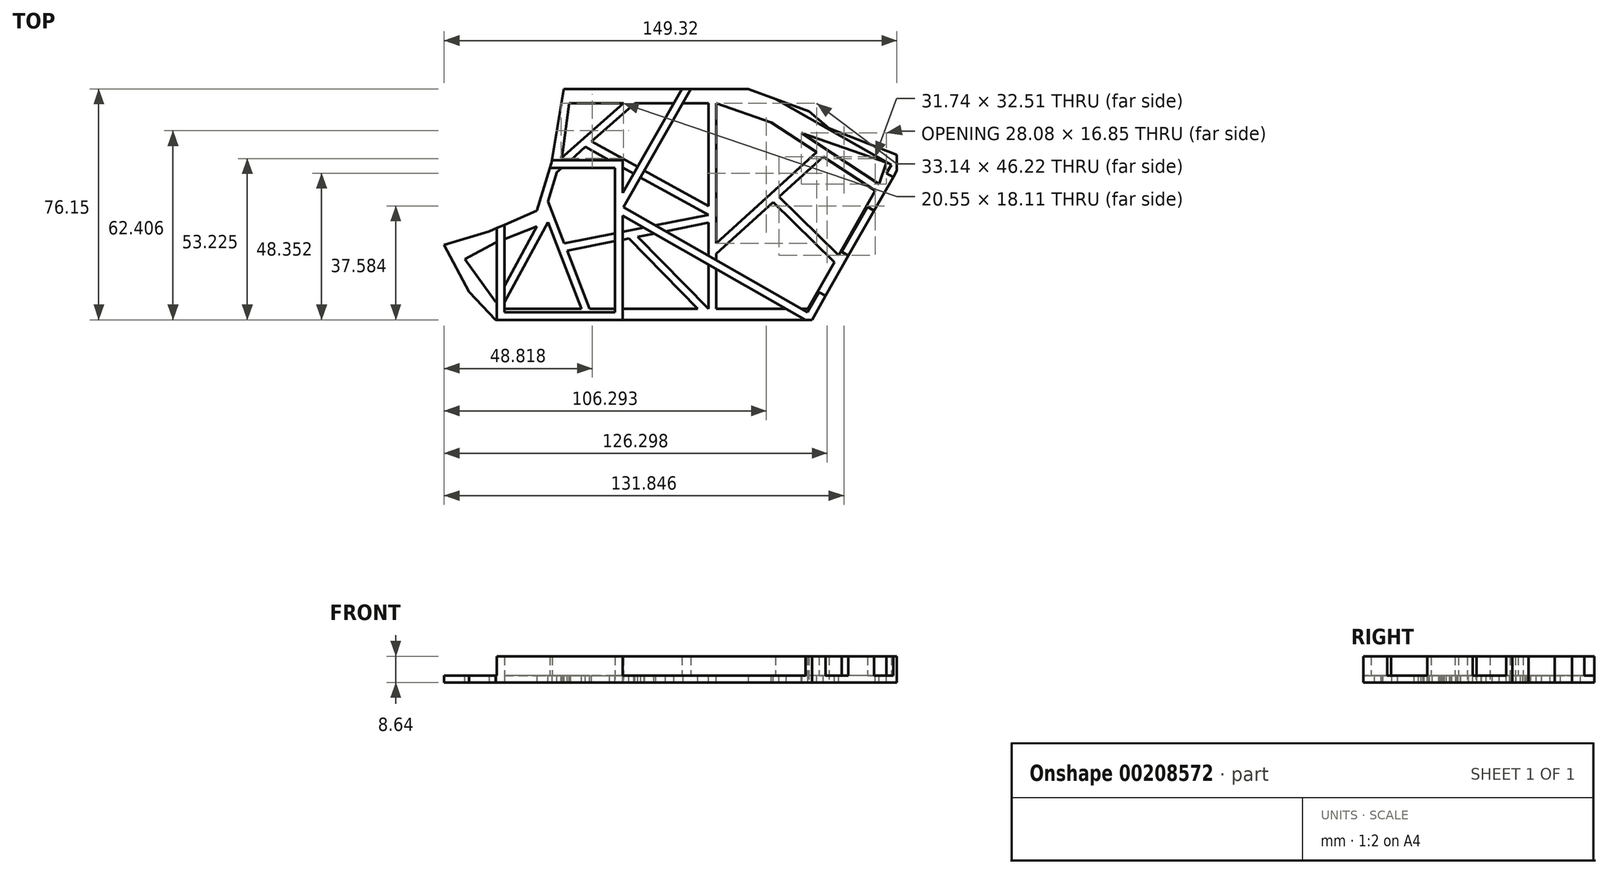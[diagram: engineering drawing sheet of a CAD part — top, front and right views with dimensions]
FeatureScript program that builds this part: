
annotation { "Feature Type Name" : "Feature", "Feature Type Description" : "" }
export const myFeature = defineFeature(function(context is Context, id is Id, definition is map)
    precondition{}
    {
        {
            var Q0;
            Q0=qCreatedBy(makeId("Top.planeOp"),FACE);
            var sketch = newSketch(context, id + "F0", { "sketchPlane" : qUnion([Q0])});
            skLineSegment(sketch, "E0", {"start": v(-31, -29.13) * mm, "end": v(-39.75, -19.88) * mm});
            skLineSegment(sketch, "E1", {"start": v(-39.75, -19.88) * mm, "end": v(-48, -4.38) * mm});
            skLineSegment(sketch, "E2", {"start": v(-48, -4.38) * mm, "end": v(-33.25, 0) * mm});
            skLineSegment(sketch, "E3", {"start": v(-33.25, 0) * mm, "end": v(-17.5, 6.88) * mm});
            skLineSegment(sketch, "E4", {"start": v(-17.5, 6.88) * mm, "end": v(-12.44, 23.38) * mm});
            skLineSegment(sketch, "E5", {"start": v(-12.44, 23.38) * mm, "end": v(-10.46, 47.02) * mm});
            skLineSegment(sketch, "E6", {"start": v(-10.46, 47.02) * mm, "end": v(19.98, 47.02) * mm});
            skLineSegment(sketch, "E7", {"start": v(19.98, 47.02) * mm, "end": v(21.89, 47.02) * mm});
            skLineSegment(sketch, "E8", {"start": v(21.89, 47.02) * mm, "end": v(52.33, 47.02) * mm});
            skLineSegment(sketch, "E9", {"start": v(50.42, 47.02) * mm, "end": v(52.33, 47.02) * mm});
            skLineSegment(sketch, "E10", {"start": v(78.88, 34.03) * mm, "end": v(101.32, 25.34) * mm});
            skLineSegment(sketch, "E11", {"start": v(101.32, 25.34) * mm, "end": v(101.32, 20.06) * mm});
            skLineSegment(sketch, "E12", {"start": v(73.3, -29.13) * mm, "end": v(-31, -29.13) * mm});
            skLineSegment(sketch, "E13", {"start": v(-10.46, 47.02) * mm, "end": v(-10.46, 53.42) * mm});
            skLineSegment(sketch, "E14", {"start": v(-10.46, 53.42) * mm, "end": v(-8.56, 53.42) * mm});
            skLineSegment(sketch, "E15", {"start": v(-8.56, 53.42) * mm, "end": v(-8.56, 47.02) * mm});
            skLineSegment(sketch, "E16", {"start": v(19.98, 47.02) * mm, "end": v(19.98, 53.42) * mm});
            skLineSegment(sketch, "E17", {"start": v(19.98, 53.42) * mm, "end": v(21.89, 53.42) * mm});
            skLineSegment(sketch, "E18", {"start": v(21.89, 53.42) * mm, "end": v(21.89, 47.02) * mm});
            skLineSegment(sketch, "E19", {"start": v(52.33, 47.02) * mm, "end": v(53.46, 53.42) * mm});
            skLineSegment(sketch, "E20", {"start": v(50.42, 53.42) * mm, "end": v(53.46, 53.42) * mm});
            skLineSegment(sketch, "E21", {"start": v(50.42, 53.42) * mm, "end": v(50.42, 47.02) * mm});
            skLineSegment(sketch, "E22", {"start": v(101.32, 25.34) * mm, "end": v(102.22, 27.67) * mm});
            skLineSegment(sketch, "E23", {"start": v(-8.56, 47.02) * mm, "end": v(-12.44, 23.38) * mm});
            skLineSegment(sketch, "E24", {"start": v(101.32, 20.06) * mm, "end": v(73.3, -29.13) * mm});
            skLineSegment(sketch, "E25", {"start": v(52.33, 47.02) * mm, "end": v(72.33, 39.67) * mm});
            skLineSegment(sketch, "E26", {"start": v(102.22, 27.67) * mm, "end": v(103.95, 27) * mm});
            skLineSegment(sketch, "E27", {"start": v(103.95, 27) * mm, "end": v(101.32, 20.06) * mm});
            skLineSegment(sketch, "E28", {"start": v(72.33, 39.67) * mm, "end": v(78.88, 34.03) * mm});
            skSolve(sketch);
        }
        {
            var Q0;
            Q0=makeQuery(id+"F0.imprint","IMPRINT",FACE,{"disambiguationData":[TD([[makeQuery(id+"F0.imprint","IMPRINT",EDGE,{"derivedFrom":sQuery(id+"F0.wireOp",EDGE,"E0")}),-1.0]])]});
            var Q1;
            Q1=makeQuery(id+"F0.imprint","IMPRINT",FACE,{"disambiguationData":[TD([[makeQuery(id+"F0.imprint","IMPRINT",EDGE,{"derivedFrom":sQuery(id+"F0.wireOp",EDGE,"Gi2NU1hI-RyGe-3cBe-QKJR-tDSeOLIxTJu2")}),-1.0]])]});
            extrude(context, id + "F1", {"entities" : qUnion([Q0, Q1]), "depth" : 2.3 * mm});
        }
        {
            var Q0;
            Q0=makeQuery(id+"F1.opExtrude","CAP_FACE",FACE,{"disambiguationData":[OSD([sQuery(id+"F0.wireOp",EDGE,"E0"),sQuery(id+"F0.wireOp",EDGE,"E1"),sQuery(id+"F0.wireOp",EDGE,"E2"),sQuery(id+"F0.wireOp",EDGE,"E3"),sQuery(id+"F0.wireOp",EDGE,"E4"),sQuery(id+"F0.wireOp",EDGE,"E6"),sQuery(id+"F0.wireOp",EDGE,"E7"),sQuery(id+"F0.wireOp",EDGE,"E8"),sQuery(id+"F0.wireOp",EDGE,"E9"),sQuery(id+"F0.wireOp",EDGE,"E10"),sQuery(id+"F0.wireOp",EDGE,"E11"),sQuery(id+"F0.wireOp",EDGE,"E12"),sQuery(id+"F0.wireOp",EDGE,"E23"),sQuery(id+"F0.wireOp",EDGE,"E24"),sQuery(id+"F0.wireOp",EDGE,"E25"),sQuery(id+"F0.wireOp",EDGE,"E28")])],"isStart":false});
            var sketch = newSketch(context, id + "F2", { "sketchPlane" : qUnion([Q0])});
            skLineSegment(sketch, "E29", {"start": v(71.83, -26.59) * mm, "end": v(99.48, 21.97) * mm});
            skLineSegment(sketch, "E30", {"start": v(99.48, 21.97) * mm, "end": v(61.26, 43.74) * mm});
            skLineSegment(sketch, "E31", {"start": v(72.33, 39.67) * mm, "end": v(101.32, 25.34) * mm});
            skLineSegment(sketch, "E32", {"start": v(72.33, 39.67) * mm, "end": v(61.26, 43.74) * mm});
            skLineSegment(sketch, "E33", {"start": v(71.83, -26.59) * mm, "end": v(11.13, 7.98) * mm});
            skLineSegment(sketch, "E34", {"start": v(8.37, 21.04) * mm, "end": v(8.37, -26.59) * mm});
            skLineSegment(sketch, "E35", {"start": v(8.37, 21.04) * mm, "end": v(-28.14, 21.04) * mm});
            skLineSegment(sketch, "E36", {"start": v(-28.14, 21.04) * mm, "end": v(-28.14, -26.59) * mm});
            skLineSegment(sketch, "E37", {"start": v(-28.14, -29.13) * mm, "end": v(8.37, -29.13) * mm});
            skLineSegment(sketch, "E38", {"start": v(-30.68, -29.13) * mm, "end": v(-30.68, 23.58) * mm});
            skLineSegment(sketch, "E39", {"start": v(-30.68, 23.58) * mm, "end": v(10.9, 23.58) * mm});
            skLineSegment(sketch, "E40", {"start": v(-28.14, -29.13) * mm, "end": v(-30.68, -29.13) * mm});
            skLineSegment(sketch, "E41", {"start": v(10.9, -29.13) * mm, "end": v(8.37, -29.13) * mm});
            skLineSegment(sketch, "E42", {"start": v(52.33, 47.02) * mm, "end": v(61.26, 43.74) * mm});
            skLineSegment(sketch, "E43", {"start": v(101.32, 25.34) * mm, "end": v(101.32, 20.06) * mm});
            skLineSegment(sketch, "E44", {"start": v(101.32, 20.06) * mm, "end": v(73.3, -29.13) * mm});
            skLineSegment(sketch, "E45", {"start": v(73.3, -29.13) * mm, "end": v(71.16, -29.13) * mm});
            skPoint(sketch, "E46.startSnap0", {"position": v(-25.38, 3.44) * mm});
            skLineSegment(sketch, "E47", {"start": v(-12.38, 23.58) * mm, "end": v(-13.16, 21.04) * mm});
            skLineSegment(sketch, "E48", {"start": v(8.37, -29.13) * mm, "end": v(10.9, -29.13) * mm});
            skPoint(sketch, "E49.orphan", {"position": v(8.37, 9.55) * mm});
            skLineSegment(sketch, "E50", {"start": v(-28.14, 2.23) * mm, "end": v(-30.68, 1.12) * mm});
            skLineSegment(sketch, "E51", {"start": v(71.16, -29.13) * mm, "end": v(10.9, 5.19) * mm});
            skLineSegment(sketch, "E52.trimOffspring", {"start": v(10.9, 5.19) * mm, "end": v(10.9, -29.13) * mm});
            skLineSegment(sketch, "E53", {"start": v(10.9, 23.58) * mm, "end": v(10.9, 12.72) * mm});
            skLineSegment(sketch, "E54", {"start": v(30.44, 47.02) * mm, "end": v(10.9, 12.72) * mm});
            skLineSegment(sketch, "E55", {"start": v(11.13, 7.98) * mm, "end": v(33.37, 47.02) * mm});
            skLineSegment(sketch, "E56", {"start": v(33.37, 47.02) * mm, "end": v(30.44, 47.02) * mm});
            skLineSegment(sketch, "E57", {"start": v(100.12, 17.96) * mm, "end": v(97.91, 19.21) * mm});
            skLineSegment(sketch, "E58", {"start": v(93.83, 6.92) * mm, "end": v(91.63, 8.18) * mm});
            skLineSegment(sketch, "E59", {"start": v(85.35, -7.98) * mm, "end": v(83.14, -6.72) * mm});
            skLineSegment(sketch, "E60", {"start": v(77.8, -21.22) * mm, "end": v(75.6, -19.96) * mm});
            skLineSegment(sketch, "E61", {"start": v(-28.14, -26.59) * mm, "end": v(8.37, -26.59) * mm});
            skSolve(sketch);
        }
        {
            var Q0;
            {var subQ0=sQuery(id+"F0.wireOp",EDGE,"E1");Q0=makeQuery(id+"FvVTFxztvHye57Z_1.boolean.opBoolean","MERGE",FACE,{"derivedFrom":[makeQuery(id+"F1.opExtrude","CAP_FACE",FACE,{"disambiguationData":[OSD([sQuery(id+"F0.wireOp",EDGE,"E0"),subQ0,sQuery(id+"F0.wireOp",EDGE,"E2"),sQuery(id+"F0.wireOp",EDGE,"E3"),sQuery(id+"F0.wireOp",EDGE,"E4"),sQuery(id+"F0.wireOp",EDGE,"E6"),sQuery(id+"F0.wireOp",EDGE,"E7"),sQuery(id+"F0.wireOp",EDGE,"E8"),sQuery(id+"F0.wireOp",EDGE,"E9"),sQuery(id+"F0.wireOp",EDGE,"E10"),sQuery(id+"F0.wireOp",EDGE,"E11"),sQuery(id+"F0.wireOp",EDGE,"E12"),sQuery(id+"F0.wireOp",EDGE,"E23"),sQuery(id+"F0.wireOp",EDGE,"E24"),sQuery(id+"F0.wireOp",EDGE,"E25"),sQuery(id+"F0.wireOp",EDGE,"fd09a7df-8c5c-424c-a2e8-465319626604.filletArc"),sQuery(id+"F0.wireOp",EDGE,"Gi2NU1hI-RyGe-3cBe-QKJR-tDSeOLIxTJu2"),sQuery(id+"F0.wireOp",EDGE,"a5mEmpnJ-nNCN-zs6l-W8Vb-FC9yOFSv0VO3"),sQuery(id+"F0.wireOp",EDGE,"UyYbmhtn-IZG5-9lsr-55o4-O6naXDKF2BvH"),sQuery(id+"F0.wireOp",EDGE,"27fbc29f-c9e2-412b-bed3-38be6e3044b4.trimOffspring")])],"isStart":false}),makeQuery(id+"FvVTFxztvHye57Z_1.opExtrude","SWEPT_FACE",FACE,{"disambiguationData":[OSD([subQ0]),TDD([makeQuery(id+"F1.opExtrude","CAP_EDGE",EDGE,{"disambiguationData":[OSD([subQ0])],"isStart":false})])]})]});}
            var sketch = newSketch(context, id + "F3", { "sketchPlane" : qUnion([Q0])});
            skLineSegment(sketch, "E62", {"start": v(-6.84, 42.33) * mm, "end": v(41.72, 42.33) * mm});
            skLineSegment(sketch, "E63", {"start": v(41.72, 42.33) * mm, "end": v(97.89, 22.71) * mm});
            skLineSegment(sketch, "E64", {"start": v(97.89, 22.71) * mm, "end": v(95.43, 15.67) * mm});
            skLineSegment(sketch, "E65", {"start": v(95.43, 15.67) * mm, "end": v(71.96, -25.53) * mm});
            skLineSegment(sketch, "E66", {"start": v(71.96, -25.53) * mm, "end": v(-29.35, -25.53) * mm});
            skLineSegment(sketch, "E67", {"start": v(-29.35, -25.53) * mm, "end": v(-41.2, -9.08) * mm});
            skLineSegment(sketch, "E68", {"start": v(-41.2, -9.08) * mm, "end": v(-31, -3.66) * mm});
            skLineSegment(sketch, "E69", {"start": v(-31, -3.66) * mm, "end": v(-13.83, 3.07) * mm});
            skLineSegment(sketch, "E70", {"start": v(-13.83, 3.07) * mm, "end": v(-13.77, 9.94) * mm});
            skLineSegment(sketch, "E71", {"start": v(-13.83, 3.07) * mm, "end": v(-29.35, -25.53) * mm});
            skLineSegment(sketch, "E72", {"start": v(-17.5, 1.63) * mm, "end": v(-31, -23.25) * mm});
            skLineSegment(sketch, "E73", {"start": v(-13.83, 3.07) * mm, "end": v(-2.72, -25.53) * mm});
            skLineSegment(sketch, "E74", {"start": v(0, -25.53) * mm, "end": v(-13.77, 9.94) * mm});
            skLineSegment(sketch, "E75", {"start": v(-9.46, 24.22) * mm, "end": v(11.1, 42.33) * mm});
            skLineSegment(sketch, "E76", {"start": v(-10.85, 19.6) * mm, "end": v(14.93, 42.33) * mm});
            skLineSegment(sketch, "E77", {"start": v(95.43, 15.67) * mm, "end": v(69.8, 32.52) * mm});
            skLineSegment(sketch, "E78", {"start": v(94.17, 13.46) * mm, "end": v(59.95, 35.96) * mm});
            skLineSegment(sketch, "E79", {"start": v(41.72, 42.33) * mm, "end": v(41.72, -25.53) * mm});
            skLineSegment(sketch, "E80", {"start": v(39.18, 42.33) * mm, "end": v(39.18, -25.53) * mm});
            skLineSegment(sketch, "E81", {"start": v(0.61, 29.7) * mm, "end": v(39.18, 8.4) * mm});
            skLineSegment(sketch, "E82", {"start": v(-1.41, 27.92) * mm, "end": v(39.18, 5.5) * mm});
            skLineSegment(sketch, "E83", {"start": v(-8.39, -3.92) * mm, "end": v(39.18, 5.5) * mm});
            skPoint(sketch, "E84.endSnap0", {"position": v(-6.89, -7.8) * mm});
            skLineSegment(sketch, "E85", {"start": v(74.87, 26.15) * mm, "end": v(41.72, -3.89) * mm});
            skLineSegment(sketch, "E86", {"start": v(77.06, 24.71) * mm, "end": v(41.72, -7.32) * mm});
            skLineSegment(sketch, "E87", {"start": v(82.06, -7.8) * mm, "end": v(62.43, 11.45) * mm});
            skLineSegment(sketch, "E88", {"start": v(60.54, 9.74) * mm, "end": v(80.76, -10.08) * mm});
            skLineSegment(sketch, "E89", {"start": v(39.18, 2.9) * mm, "end": v(-7.46, -6.33) * mm});
            skLineSegment(sketch, "E90", {"start": v(39.18, -25.53) * mm, "end": v(15.86, -1.71) * mm});
            skLineSegment(sketch, "E91", {"start": v(35.63, -25.53) * mm, "end": v(12.89, -2.3) * mm});
            skPoint(sketch, "E92", {"position": v(-6.84, 42.33) * mm});
            skPoint(sketch, "E93.orphan", {"position": v(-13.71, 17.09) * mm});
            skLineSegment(sketch, "E94", {"start": v(-6.84, 42.33) * mm, "end": v(-8.89, 26.11) * mm});
            skLineSegment(sketch, "E95", {"start": v(-8.89, 26.11) * mm, "end": v(-13.77, 9.94) * mm});
            skPoint(sketch, "E96", {"position": v(41.72, -3.89) * mm});
            skSolve(sketch);
        }
        {
            var Q0;
            {var subQ3=sQuery(id+"F3.wireOp",EDGE,"E82");Q0=makeQuery(id+"F3.imprint","IMPRINT",FACE,{"disambiguationData":[TD([[makeQuery(id+"F3.imprint","IMPRINT",EDGE,{"derivedFrom":subQ3}),-1.0]])]});}
            var Q1;
            {var subQ0=sQuery(id+"F3.wireOp",EDGE,"XW1hXaPo-RyUY-air6-Wdwl-tk0w2k2kVIwS");Q1=makeQuery(id+"F3.imprint","IMPRINT",FACE,{"disambiguationData":[TD([[makeQuery(id+"F3.imprint","IMPRINT",EDGE,{"derivedFrom":subQ0}),-1.0]])]});}
            var Q2;
            {var subQ5=sQuery(id+"F3.wireOp",EDGE,"E81");Q2=makeQuery(id+"F3.imprint","IMPRINT",FACE,{"disambiguationData":[TD([[makeQuery(id+"F3.imprint","IMPRINT",EDGE,{"derivedFrom":subQ5}),1.0]])]});}
            var Q3;
            {var subQ5=sQuery(id+"F3.wireOp",EDGE,"E85");Q3=makeQuery(id+"F3.imprint","IMPRINT",FACE,{"disambiguationData":[TD([[makeQuery(id+"F3.imprint","IMPRINT",EDGE,{"derivedFrom":subQ5}),-1.0]])]});}
            var Q4;
            {var subQ3=sQuery(id+"F3.wireOp",EDGE,"E87");Q4=makeQuery(id+"F3.imprint","IMPRINT",FACE,{"disambiguationData":[TD([[makeQuery(id+"F3.imprint","IMPRINT",EDGE,{"derivedFrom":subQ3}),-1.0]])]});}
            var Q5;
            {var subQ0=sQuery(id+"F3.wireOp",EDGE,"E64");Q5=makeQuery(id+"F3.imprint","IMPRINT",FACE,{"disambiguationData":[TD([[makeQuery(id+"F3.imprint","IMPRINT",EDGE,{"derivedFrom":subQ0}),-1.0]])]});}
            var Q6;
            {var subQ7=sQuery(id+"F3.wireOp",EDGE,"E88");Q6=makeQuery(id+"F3.imprint","IMPRINT",FACE,{"disambiguationData":[TD([[makeQuery(id+"F3.imprint","IMPRINT",EDGE,{"derivedFrom":subQ7}),-1.0]])]});}
            var Q7;
            {var subQ0=sQuery(id+"F3.wireOp",EDGE,"E90");Q7=makeQuery(id+"F3.imprint","IMPRINT",FACE,{"disambiguationData":[TD([[makeQuery(id+"F3.imprint","IMPRINT",EDGE,{"derivedFrom":subQ0}),-1.0]])]});}
            var Q8;
            {var subQ3=sQuery(id+"F3.wireOp",EDGE,"E91");Q8=makeQuery(id+"F3.imprint","IMPRINT",FACE,{"disambiguationData":[TD([[makeQuery(id+"F3.imprint","IMPRINT",EDGE,{"derivedFrom":subQ3}),1.0]])]});}
            var Q9;
            {var subQ0=sQuery(id+"F3.wireOp",EDGE,"E71");Q9=makeQuery(id+"F3.imprint","IMPRINT",FACE,{"disambiguationData":[TD([[makeQuery(id+"F3.imprint","IMPRINT",EDGE,{"derivedFrom":subQ0}),1.0]])]});}
            var Q10;
            {var subQ0=sQuery(id+"F3.wireOp",EDGE,"E68");Q10=makeQuery(id+"F3.imprint","IMPRINT",FACE,{"disambiguationData":[TD([[makeQuery(id+"F3.imprint","IMPRINT",EDGE,{"derivedFrom":subQ0}),-1.0]])]});}
            var Q11;
            {var subQ2=sQuery(id+"F3.wireOp",EDGE,"E75");Q11=makeQuery(id+"F3.imprint","IMPRINT",FACE,{"disambiguationData":[TD([[makeQuery(id+"F3.imprint","IMPRINT",EDGE,{"derivedFrom":subQ2}),1.0]])]});}
            extrude(context, id + "F4", {"entities" : qUnion([Q0, Q1, Q2, Q3, Q4, Q5, Q6, Q7, Q8, Q9, Q10, Q11]), "operationType" : NewBodyOperationType.REMOVE, "endBound" : BoundingType.THROUGH_ALL, "oppositeDirection" : true, "depth" : 25.4 * mm});
        }
        {
            var Q0;
            {var subQ0=sQuery(id+"F2.wireOp",EDGE,"E40");Q0=makeQuery(id+"F2.imprint","IMPRINT",FACE,{"disambiguationData":[TD([[makeQuery(id+"F2.imprint","IMPRINT",EDGE,{"derivedFrom":subQ0}),-1.0]])]});}
            var Q1;
            {var subQ9=sQuery(id+"F2.wireOp",EDGE,"E33");Q1=makeQuery(id+"F2.imprint","IMPRINT",FACE,{"disambiguationData":[TD([[makeQuery(id+"F2.imprint","IMPRINT",EDGE,{"derivedFrom":subQ9}),1.0]])]});}
            var Q2;
            {var subQ0=sQuery(id+"F2.wireOp",EDGE,"E58");Q2=makeQuery(id+"F2.imprint","IMPRINT",FACE,{"disambiguationData":[TD([[makeQuery(id+"F2.imprint","IMPRINT",EDGE,{"derivedFrom":subQ0}),1.0]])]});}
            var Q3;
            {var subQ1=sQuery(id+"F2.wireOp",EDGE,"E30");Q3=makeQuery(id+"F2.imprint","IMPRINT",FACE,{"disambiguationData":[TD([[makeQuery(id+"F2.imprint","IMPRINT",EDGE,{"derivedFrom":subQ1}),-1.0]])]});}
            extrude(context, id + "F5", {"entities" : qUnion([Q0, Q1, Q2, Q3]), "operationType" : NewBodyOperationType.ADD, "depth" : 6.35 * mm, "hasSecondDirection" : true, "secondDirectionOppositeDirection" : true, "secondDirectionDepth" : 2.3 * mm});
        }
    });
